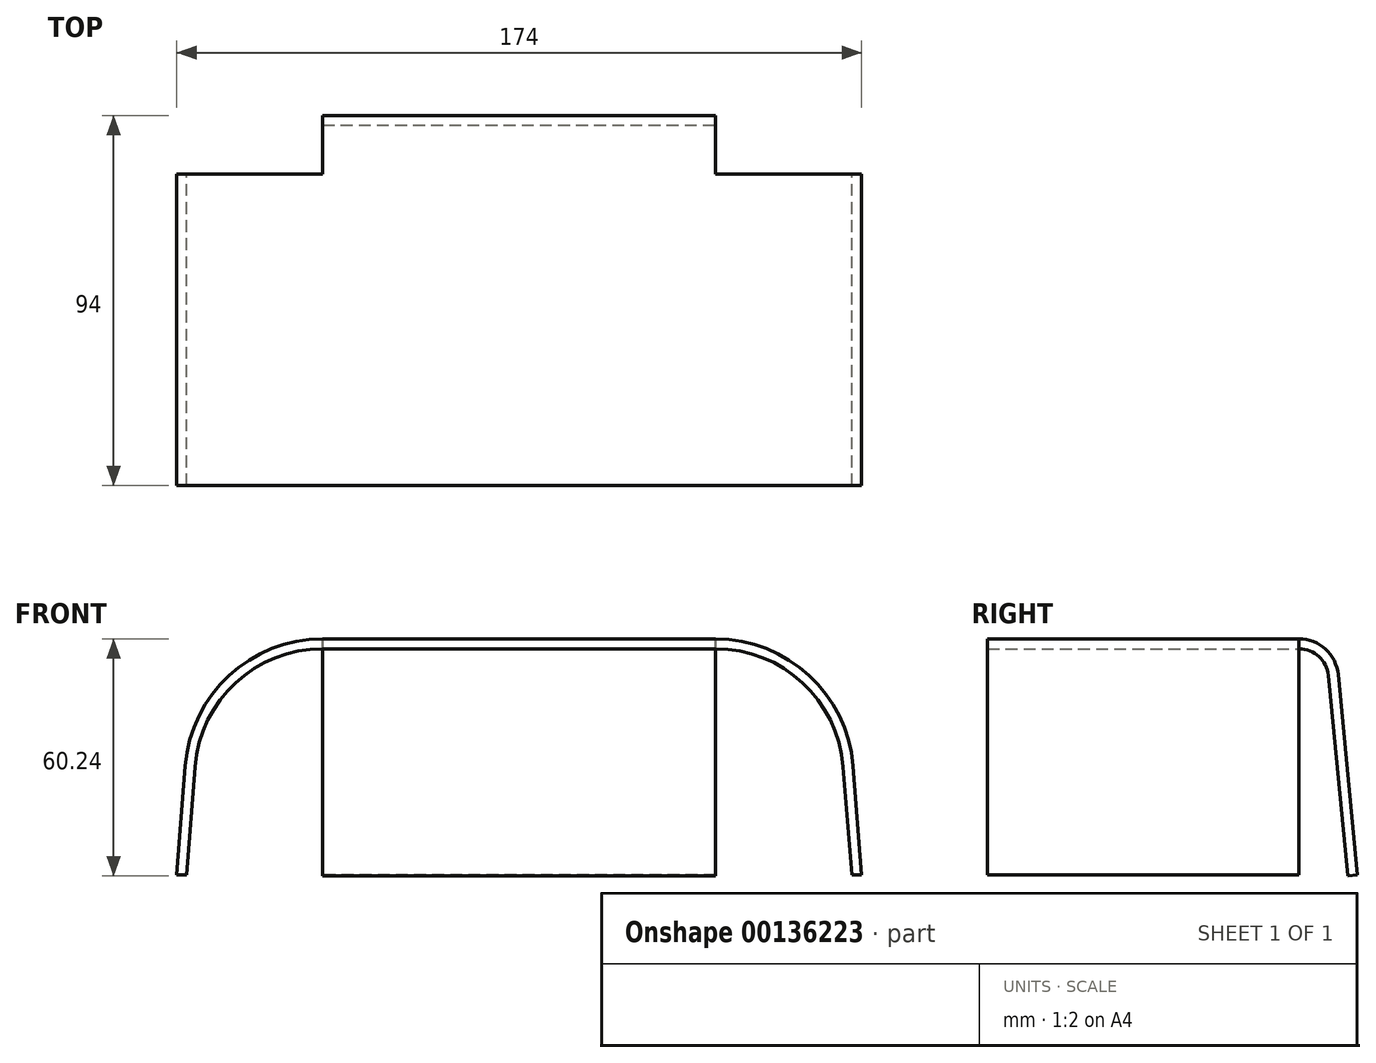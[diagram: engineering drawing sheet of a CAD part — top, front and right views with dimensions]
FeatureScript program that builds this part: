
annotation { "Feature Type Name" : "Feature", "Feature Type Description" : "" }
export const myFeature = defineFeature(function(context is Context, id is Id, definition is map)
    precondition{}
    {
        {
            var Q0;
            Q0=qCreatedBy(makeId("Front.planeOp"),FACE);
            var sketch = newSketch(context, id + "F0", { "sketchPlane" : qUnion([Q0])});
            skLineSegment(sketch, "E0", {"start": v(-87, 0) * mm, "end": v(0, 0) * mm, "construction": true});
            skLineSegment(sketch, "E1", {"start": v(-87, 0) * mm, "end": v(-84.82, 27.75) * mm, "construction": true});
            skLineSegment(sketch, "E2", {"start": v(-49.92, 60) * mm, "end": v(0, 60) * mm, "construction": true});
            skPoint(sketch, "E3.visualSharp", {"position": v(-82.28, 60) * mm});
            skLineSegment(sketch, "E4", {"start": v(-87, 0) * mm, "end": v(-84.82, 27.75) * mm});
            skLineSegment(sketch, "E5", {"start": v(-49.92, 60) * mm, "end": v(0, 60) * mm});
            skArc(sketch, "E6.filletArc", {"start": v(-49.92, 60) * mm, "mid": v(-73.68, 50.7) * mm, "end": v(-84.82, 27.75) * mm});
            skLineSegment(sketch, "E7.0", {"start": v(-84.5, 0) * mm, "end": v(-82.32, 27.55) * mm});
            skArc(sketch, "E7.1", {"start": v(-49.92, 57.5) * mm, "mid": v(-71.99, 48.87) * mm, "end": v(-82.32, 27.55) * mm});
            skLineSegment(sketch, "E7.2", {"start": v(-49.92, 57.5) * mm, "end": v(0, 57.5) * mm});
            skPoint(sketch, "E8.MirrorCS.end.orphan", {"position": v(0, 60) * mm});
            skLineSegment(sketch, "E9.MirrorCS", {"start": v(49.92, 57.5) * mm, "end": v(0, 57.5) * mm});
            skLineSegment(sketch, "E10.MirrorCS", {"start": v(49.92, 60) * mm, "end": v(0, 60) * mm});
            skArc(sketch, "E11.MirrorCS", {"start": v(49.92, 57.5) * mm, "mid": v(71.99, 48.87) * mm, "end": v(82.32, 27.55) * mm});
            skArc(sketch, "E12.MirrorCS", {"start": v(49.92, 60) * mm, "mid": v(73.68, 50.7) * mm, "end": v(84.82, 27.75) * mm});
            skLineSegment(sketch, "E13.MirrorCS", {"start": v(84.5, 0) * mm, "end": v(82.32, 27.55) * mm});
            skLineSegment(sketch, "E14.MirrorCS", {"start": v(87, 0) * mm, "end": v(84.82, 27.75) * mm});
            skLineSegment(sketch, "E15.MirrorCS", {"start": v(87, 0) * mm, "end": v(0, 0) * mm, "construction": true});
            skLineSegment(sketch, "E16", {"start": v(-87, 0) * mm, "end": v(-84.5, 0) * mm});
            skLineSegment(sketch, "E17", {"start": v(87, 0) * mm, "end": v(84.5, 0) * mm});
            skSolve(sketch);
        }
        {
            var Q0;
            Q0=qCreatedBy(makeId("Top.planeOp"),FACE);
            var sketch = newSketch(context, id + "F1", { "sketchPlane" : qUnion([Q0])});
            skLineSegment(sketch, "E18", {"start": v(-85.95, 0) * mm, "end": v(-85.95, 94) * mm});
            skLineSegment(sketch, "E19.MirrorCS", {"start": v(85.95, 0) * mm, "end": v(85.95, 94) * mm});
            skLineSegment(sketch, "E20", {"start": v(85.95, 94) * mm, "end": v(-85.95, 94) * mm});
            skSolve(sketch);
        }
        {
            var Q0;
            Q0=qCreatedBy(makeId("Right.planeOp"),FACE);
            var sketch = newSketch(context, id + "F2", { "sketchPlane" : qUnion([Q0])});
            skLineSegment(sketch, "E21", {"start": v(0, 60) * mm, "end": v(79.14, 60) * mm});
            skLineSegment(sketch, "E22", {"start": v(89.1, 50.96) * mm, "end": v(94, 0) * mm});
            skPoint(sketch, "E23.visualSharp", {"position": v(88.22, 60) * mm});
            skArc(sketch, "E23.filletArc", {"start": v(89.1, 50.96) * mm, "mid": v(85.86, 57.4) * mm, "end": v(79.14, 60) * mm});
            skLineSegment(sketch, "E24.0", {"start": v(86.6, 50.72) * mm, "end": v(91.51, -0.24) * mm});
            skArc(sketch, "E24.1", {"start": v(86.6, 50.72) * mm, "mid": v(84.18, 55.55) * mm, "end": v(79.14, 57.5) * mm});
            skLineSegment(sketch, "E24.2", {"start": v(0, 57.5) * mm, "end": v(79.14, 57.5) * mm});
            skSolve(sketch);
        }
        {
            var Q0;
            Q0=makeQuery(id+"F0.imprint","IMPRINT",FACE,{"disambiguationData":[TD([[makeQuery(id+"F0.imprint","IMPRINT",EDGE,{"derivedFrom":sQuery(id+"F0.wireOp",EDGE,"E4")}),-1.0]])]});
            var Q1;
            Q1=sQuery(id+"F2.wireOp",EDGE,"E21");
            sweep(context, id + "F3", {"profiles" : qUnion([Q0]), "path" : qUnion([Q1])});
        }
        {
            var Q0;
            Q0=makeQuery(id+"F3.opSweep","CAP_FACE",FACE,{"disambiguationData":[OSD([sQuery(id+"F0.wireOp",EDGE,"E4"),sQuery(id+"F0.wireOp",EDGE,"E5"),sQuery(id+"F0.wireOp",EDGE,"E6.filletArc"),sQuery(id+"F0.wireOp",EDGE,"E7.0"),sQuery(id+"F0.wireOp",EDGE,"E7.1"),sQuery(id+"F0.wireOp",EDGE,"E7.2"),sQuery(id+"F0.wireOp",EDGE,"E9.MirrorCS"),sQuery(id+"F0.wireOp",EDGE,"E10.MirrorCS"),sQuery(id+"F0.wireOp",EDGE,"E11.MirrorCS"),sQuery(id+"F0.wireOp",EDGE,"E12.MirrorCS"),sQuery(id+"F0.wireOp",EDGE,"E13.MirrorCS"),sQuery(id+"F0.wireOp",EDGE,"E14.MirrorCS"),sQuery(id+"F0.wireOp",EDGE,"E16"),sQuery(id+"F0.wireOp",EDGE,"E17"),sQuery(id+"F2.wireOp",VERTEX,"E21.end")])],"isStart":false});
            var sketch = newSketch(context, id + "F4", { "sketchPlane" : qUnion([Q0])});
            skLineSegment(sketch, "E25.bottom", {"start": v(-49.92, 57.5) * mm, "end": v(49.92, 57.5) * mm});
            skLineSegment(sketch, "E25.top", {"start": v(-49.92, 60) * mm, "end": v(49.92, 60) * mm});
            skLineSegment(sketch, "E25.left", {"start": v(-49.92, 57.5) * mm, "end": v(-49.92, 60) * mm});
            skLineSegment(sketch, "E25.right", {"start": v(49.92, 57.5) * mm, "end": v(49.92, 60) * mm});
            skSolve(sketch);
        }
        {
            var Q0;
            Q0=makeQuery(id+"F4.imprint","IMPRINT",FACE,{"disambiguationData":[TD([[makeQuery(id+"F4.imprint","IMPRINT",EDGE,{"derivedFrom":sQuery(id+"F4.wireOp",EDGE,"E25.bottom")}),1.0]])]});
            var Q1;
            Q1=sQuery(id+"F2.wireOp",EDGE,"E23.filletArc");
            var Q2;
            Q2=sQuery(id+"F2.wireOp",EDGE,"E22");
            sweep(context, id + "F5", {"operationType" : NewBodyOperationType.ADD, "profiles" : qUnion([Q0]), "path" : qUnion([Q1, Q2])});
        }
    });
